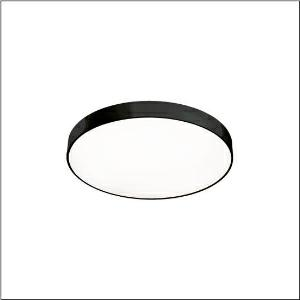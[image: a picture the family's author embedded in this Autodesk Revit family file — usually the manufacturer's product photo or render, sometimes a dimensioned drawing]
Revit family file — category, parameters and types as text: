
# Revit family: round_21_m_51mr36gd0421b
name_source: partatom
category: Lighting Fixtures
units: mm (PartAtom-declared; Revit-internal decimal feet)

## family parameters
Cut with Voids When Loaded = No
Host = Face
Light Source = No
Part Type = Normal
Room Calculation Point = No
Round Connector Dimension = Use Diameter
Shared = No

## types (1)
- Round 21 M (1 x LED, 7160 lm, 54.5 W, 4000K)
    Apparent Load = 55 VA
    CIE Flux Codes = 49 80 96 85 100
    Color Rendering = 80
    Color Temperature = 4000K
    Default Elevation = 1800 mm
    Description = Round 21 M, wall and ceiling luminaire, primary optical cover: cover, of PMMA, opal, light emission: direct/indirect distribution, primary light characteristic: symmetric, installation type: suspended mounting, surface-mounted, LED, rated luminous flux: 7.110lm, luminous efficacy: 130lm/W, light colour: 840, colour temperature: 4000K, with terminal, 5-pole, mains connection: 230V, AC, 50/60Hz, rated input power: 55W, housing, of aluminium, coated, black, diameter: 600mm, height: 62mm, protection rating (complete): IP40, insulation class (complete): insulation class I (protective earthing), certification: CE, impact resistance: IK04, permissible operating ambient temperature: -10..+35°C, packaging unit: 1 piece
    Height = 87 mm
    Lamp = 1 x LED
    Lamp Light Flux = 7160 lm
    Lamp Power = 54.5 W
    Lamp count = 1
    Length = 600 mm
    Luminous efficacy = 131 lm/W
    Manufacturer = Siteco
    ModVariant = No
    Model = 51MR36GD0421B
    Mounting Place = Ceiling
    Mounting Type = Surface mounted
    Number of Poles = 1
    OnlyDefault = Yes
    Power Factor = 1
    Product Name = Round 21 M
    Product group = wall and ceiling luminaire
    ProductGroupID = 301
    Protection Class = Protection class I
    Protection Degree = IP 40
    RLX_Detail_Level = 1
    RLX_Emergency_Light_Flux = 0 lm
    RLX_Emergency_Type = 0
    RLX_Emergency_Type_DB = No
    RlxData = <blob elided: 18109 chars, md5=6b2ac303>
    Socket = socket
    Standby Power = 0 W
    System Light Flux = 7160 lm
    System Power = 55 W
    Type Comments = Product without accessories
    Type Image = l_1258332.jpg
    URL = http://relux.com
    VarID = ---
    Voltage = 0 V
    Weight = 0.00 kg
    Width = 0 mm  [stored 0 ft]

note: [stored X ft] marks values corroborated as IEEE doubles in the binary element streams (Revit-internal decimal feet)

## geometry (parser evidence)
native form markers: Blend x4, Sweep x11
no freeform markers — native parametric forms only
